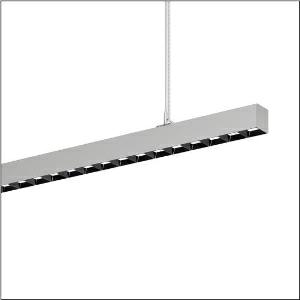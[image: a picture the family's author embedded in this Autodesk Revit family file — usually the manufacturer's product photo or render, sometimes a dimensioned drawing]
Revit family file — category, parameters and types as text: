
# Revit family: silica_r__21_51mx31dc4dsb_9913
name_source: partatom
category: Lighting Fixtures
units: mm (PartAtom-declared; Revit-internal decimal feet)

## family parameters
Cut with Voids When Loaded = No
Host = Face
Light Source = No
Part Type = Normal
Room Calculation Point = No
Round Connector Dimension = Use Diameter
Shared = No

## types (1)
- --- (1 x LED, 18230 lm, 105.9 W, 4000K)
    Apparent Load = 106 VA
    CIE Flux Codes = 87 99 100 59 100
    Color Rendering = 80
    Color Temperature = 4000K
    Default Elevation = 1800 mm
    Description = Silica® 21, office luminaire, primary light control with darklight reflector, of PMMA, black, CAT 2 (L<= 3000cd/m²), light emission: direct/indirect distribution, primary light characteristic: symmetric, installation type: suspended mounting, LED, rated luminous flux: 18.230lm, luminous efficacy: 172lm/W, light colour: 840, colour temperature: 4000K, control gear: DALI 2, with terminal, 3+2-pole, max. 2.5mm², mains connection: 220..240V, AC, 50/60Hz, rated input power: 105.9W, luminaire housing, of aluminium, metallic grey (RAL 9006), length: 3.004mm, width: 53mm, height: 53mm, protection rating (complete): IP20, insulation class (complete): insulation class I (protective earthing), certification: CE, permissible operating ambient temperature: 0..+35°C, standard: EN 50419, packaging unit: 1 piece
    Height = 53 mm
    Lamp = 1 x LED
    Lamp Light Flux = 18230 lm
    Lamp Power = 105.9 W
    Lamp count = 1
    Length = 3004 mm
    Luminous efficacy = 172 lm/W
    Manufacturer = Siteco
    ModVariant = No
    Model = 51MX31DC4DSB
    Mounting Place = Ceiling
    Mounting Type = Pendant
    Number of Poles = 1
    OnlyDefault = Yes
    Power Factor = 1
    Product Name = Silica® 21
    Product group = office luminaire | ceiling pendant
    ProductGroupID = 903
    Protection Class = Protection class I
    Protection Degree = IP 20
    RLX_Detail_Level = 1
    RLX_Emergency_Light_Flux = 0 lm
    RLX_Emergency_Type = 0
    RLX_Emergency_Type_DB = No
    RlxData = <blob elided: 65717 chars, md5=315fe49b>
    Socket = socket
    Standby Power = 0 W
    System Light Flux = 18230 lm
    System Power = 106 W
    Type Comments = factory setting: luminous flux: 100 % | dim-lin: 254 | 367 mA
    Type Image = l_1335859.jpg
    URL = http://relux.com
    VarID = @adj_124925
    Voltage = 0 V
    Weight = 0.00 kg
    Width = 53 mm

## geometry (parser evidence)
native form markers: Blend x4, Sweep x11
no freeform markers — native parametric forms only
